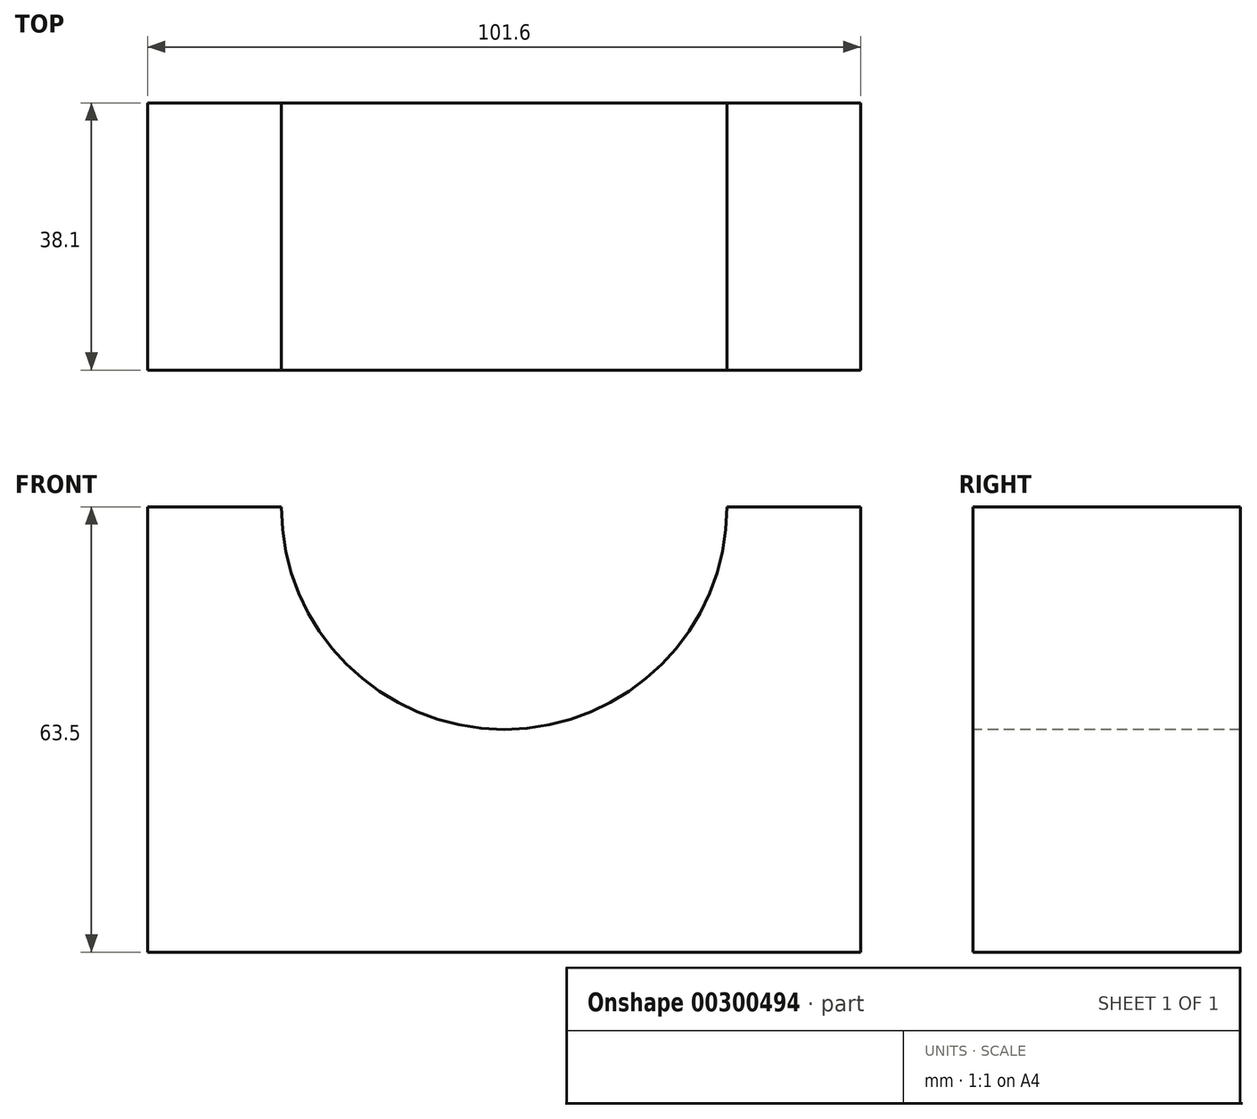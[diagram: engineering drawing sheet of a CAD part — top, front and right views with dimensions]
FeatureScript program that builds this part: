
annotation { "Feature Type Name" : "Feature", "Feature Type Description" : "" }
export const myFeature = defineFeature(function(context is Context, id is Id, definition is map)
    precondition{}
    {
        {
            var Q0;
            Q0=qCreatedBy(makeId("Front.planeOp"),FACE);
            var sketch = newSketch(context, id + "F0", { "sketchPlane" : qUnion([Q0])});
            skLineSegment(sketch, "E0.bottom", {"start": v(-50.8, 31.75) * mm, "end": v(50.8, 31.75) * mm});
            skLineSegment(sketch, "E0.top", {"start": v(-50.8, -31.75) * mm, "end": v(50.8, -31.75) * mm});
            skLineSegment(sketch, "E0.left", {"start": v(-50.8, 31.75) * mm, "end": v(-50.8, -31.75) * mm});
            skLineSegment(sketch, "E0.right", {"start": v(50.8, 31.75) * mm, "end": v(50.8, -31.75) * mm});
            skPoint(sketch, "E0.middle", {"position": v(0, 0) * mm});
            skSolve(sketch);
        }
        {
            var Q0;
            Q0=makeQuery(id+"F0.imprint","IMPRINT",FACE,{"disambiguationData":[TD([[makeQuery(id+"F0.imprint","IMPRINT",EDGE,{"derivedFrom":sQuery(id+"F0.wireOp",EDGE,"E0.bottom")}),-1.0]])]});
            extrude(context, id + "F1", {"entities" : qUnion([Q0]), "depth" : 38.1 * mm});
        }
        {
            var Q0;
            Q0=makeQuery(id+"F1.opExtrude","CAP_FACE",FACE,{"disambiguationData":[OSD([sQuery(id+"F0.wireOp",EDGE,"E0.bottom"),sQuery(id+"F0.wireOp",EDGE,"E0.top"),sQuery(id+"F0.wireOp",EDGE,"E0.left"),sQuery(id+"F0.wireOp",EDGE,"E0.right")])],"isStart":false});
            var sketch = newSketch(context, id + "F2", { "sketchPlane" : qUnion([Q0])});
            skCircle(sketch, "E1", {"center": v(0, 31.75) * mm, "radius": 31.75 * mm});
            skSolve(sketch);
        }
        {
            var Q0;
            {var subQ0=sQuery(id+"F2.wireOp",EDGE,"E1");var subQ1=makeQuery(id+"F1.opExtrude","CAP_EDGE",EDGE,{"disambiguationData":[OSD([sQuery(id+"F0.wireOp",EDGE,"E0.bottom")])],"isStart":false});var subQ2=makeQuery(id+"F2.imprint","INTERSECT",VERTEX,{"disambiguationData":[OD(0.0)],"derivedFrom":[subQ1,subQ0]});Q0=makeQuery(id+"F2.imprint","IMPRINT",FACE,{"disambiguationData":[TD([[makeQuery(id+"F2.imprint","IMPRINT",EDGE,{"disambiguationData":[TD([[subQ2,-1.0]])],"derivedFrom":subQ0}),1.0]])]});}
            extrude(context, id + "F3", {"entities" : qUnion([Q0]), "operationType" : NewBodyOperationType.REMOVE, "oppositeDirection" : true, "depth" : 50.8 * mm});
        }
    });
